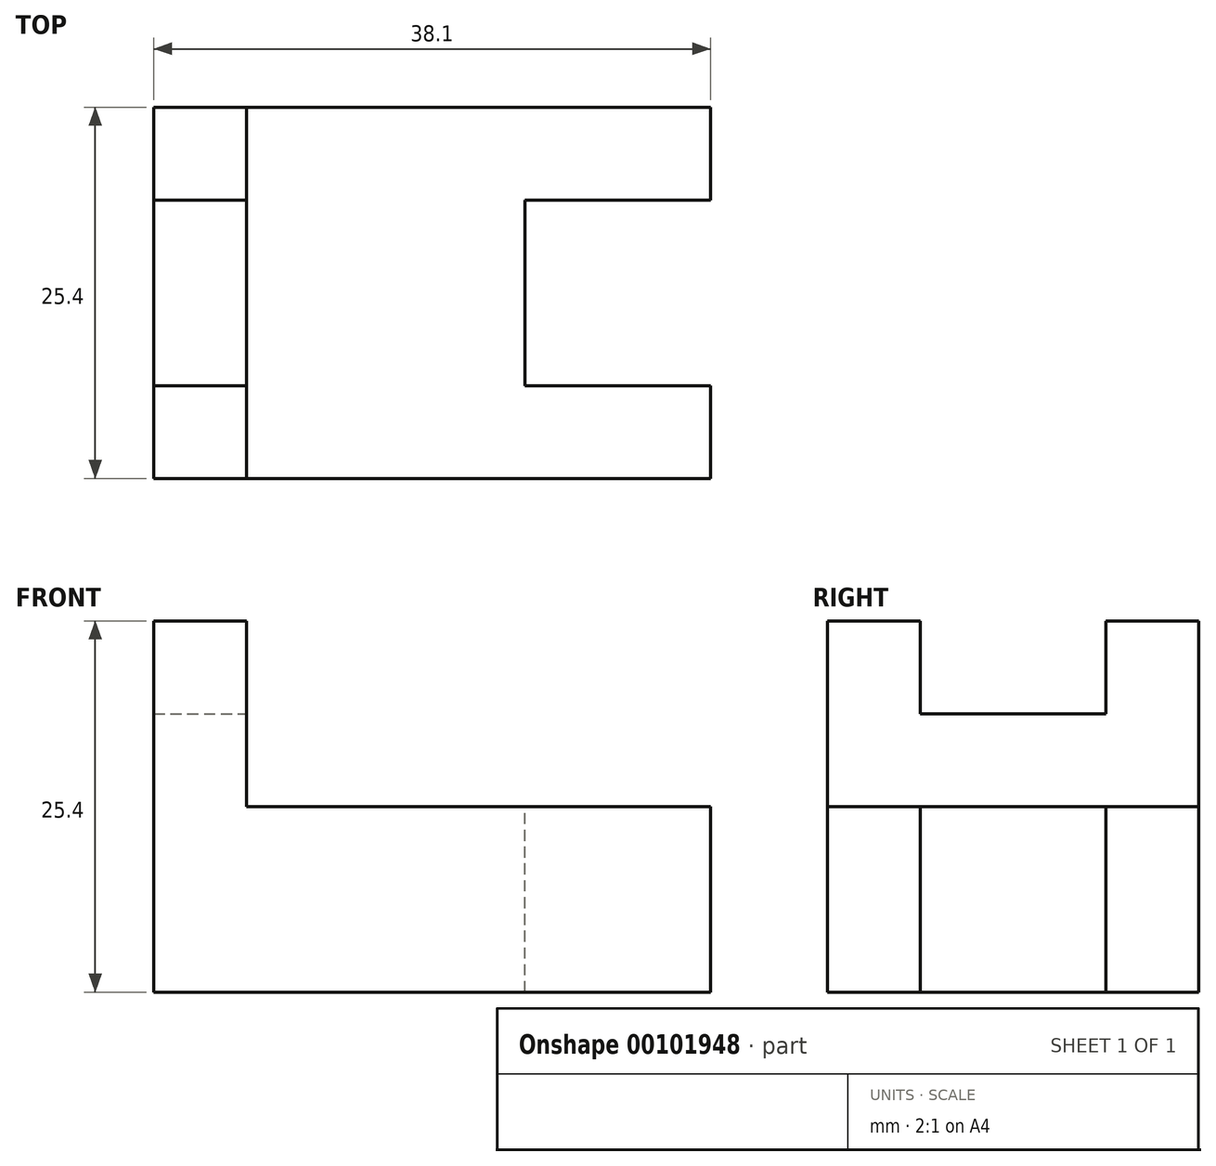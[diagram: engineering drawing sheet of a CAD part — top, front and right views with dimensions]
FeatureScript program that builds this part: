
annotation { "Feature Type Name" : "Feature", "Feature Type Description" : "" }
export const myFeature = defineFeature(function(context is Context, id is Id, definition is map)
    precondition{}
    {
        {
            var Q0;
            Q0=qCreatedBy(makeId("Front.planeOp"),FACE);
            var sketch = newSketch(context, id + "F0", { "sketchPlane" : qUnion([Q0])});
            skLineSegment(sketch, "E0.bottom", {"start": v(0, 0) * mm, "end": v(38.1, 0) * mm});
            skLineSegment(sketch, "E0.top", {"start": v(0, 25.4) * mm, "end": v(38.1, 25.4) * mm});
            skLineSegment(sketch, "E0.left", {"start": v(0, 0) * mm, "end": v(0, 25.4) * mm});
            skLineSegment(sketch, "E0.right", {"start": v(38.1, 0) * mm, "end": v(38.1, 25.4) * mm});
            skSolve(sketch);
        }
        {
            var Q0;
            Q0=makeQuery(id+"F0.imprint","IMPRINT",FACE,{"disambiguationData":[TD([[makeQuery(id+"F0.imprint","IMPRINT",EDGE,{"derivedFrom":sQuery(id+"F0.wireOp",EDGE,"E0.bottom")}),1.0]])]});
            extrude(context, id + "F1", {"entities" : qUnion([Q0]), "endBound" : BoundingType.SYMMETRIC, "depth" : 25.4 * mm});
        }
        {
            var Q0;
            Q0=qCreatedBy(makeId("Front.planeOp"),FACE);
            var sketch = newSketch(context, id + "F2", { "sketchPlane" : qUnion([Q0])});
            skLineSegment(sketch, "E1.bottom", {"start": v(38.1, 25.4) * mm, "end": v(6.35, 25.4) * mm});
            skLineSegment(sketch, "E1.top", {"start": v(38.1, 12.7) * mm, "end": v(6.35, 12.7) * mm});
            skLineSegment(sketch, "E1.left", {"start": v(38.1, 25.4) * mm, "end": v(38.1, 12.7) * mm});
            skLineSegment(sketch, "E1.right", {"start": v(6.35, 25.4) * mm, "end": v(6.35, 12.7) * mm});
            skSolve(sketch);
        }
        {
            var Q0;
            Q0 = qSketchRegion(id + "F2", true);
            extrude(context, id + "F3", {"entities" : qUnion([Q0]), "operationType" : NewBodyOperationType.REMOVE, "endBound" : BoundingType.SYMMETRIC, "oppositeDirection" : true, "depth" : 25.4 * mm});
        }
        {
            var Q0;
            Q0=qCreatedBy(makeId("Front.planeOp"),FACE);
            var sketch = newSketch(context, id + "F4", { "sketchPlane" : qUnion([Q0])});
            skLineSegment(sketch, "E2.bottom", {"start": v(38.1, 0) * mm, "end": v(25.4, 0) * mm});
            skLineSegment(sketch, "E2.top", {"start": v(38.1, 12.7) * mm, "end": v(25.4, 12.7) * mm});
            skLineSegment(sketch, "E2.left", {"start": v(38.1, 0) * mm, "end": v(38.1, 12.7) * mm});
            skLineSegment(sketch, "E2.right", {"start": v(25.4, 0) * mm, "end": v(25.4, 12.7) * mm});
            skSolve(sketch);
        }
        {
            var Q0;
            Q0 = qSketchRegion(id + "F4", true);
            extrude(context, id + "F5", {"entities" : qUnion([Q0]), "operationType" : NewBodyOperationType.REMOVE, "endBound" : BoundingType.SYMMETRIC, "depth" : 12.7 * mm});
        }
        {
            var Q0;
            Q0=qCreatedBy(makeId("Front.planeOp"),FACE);
            var sketch = newSketch(context, id + "F6", { "sketchPlane" : qUnion([Q0])});
            skLineSegment(sketch, "E3.bottom", {"start": v(0, 25.4) * mm, "end": v(6.35, 25.4) * mm});
            skLineSegment(sketch, "E3.top", {"start": v(0, 19.05) * mm, "end": v(6.35, 19.05) * mm});
            skLineSegment(sketch, "E3.left", {"start": v(0, 25.4) * mm, "end": v(0, 19.05) * mm});
            skLineSegment(sketch, "E3.right", {"start": v(6.35, 25.4) * mm, "end": v(6.35, 19.05) * mm});
            skSolve(sketch);
        }
        {
            var Q0;
            Q0=makeQuery(id+"F6.imprint","IMPRINT",FACE,{"disambiguationData":[TD([[makeQuery(id+"F6.imprint","IMPRINT",EDGE,{"derivedFrom":sQuery(id+"F6.wireOp",EDGE,"E3.bottom")}),-1.0]])]});
            extrude(context, id + "F7", {"entities" : qUnion([Q0]), "operationType" : NewBodyOperationType.REMOVE, "endBound" : BoundingType.SYMMETRIC, "depth" : 12.7 * mm});
        }
    });
